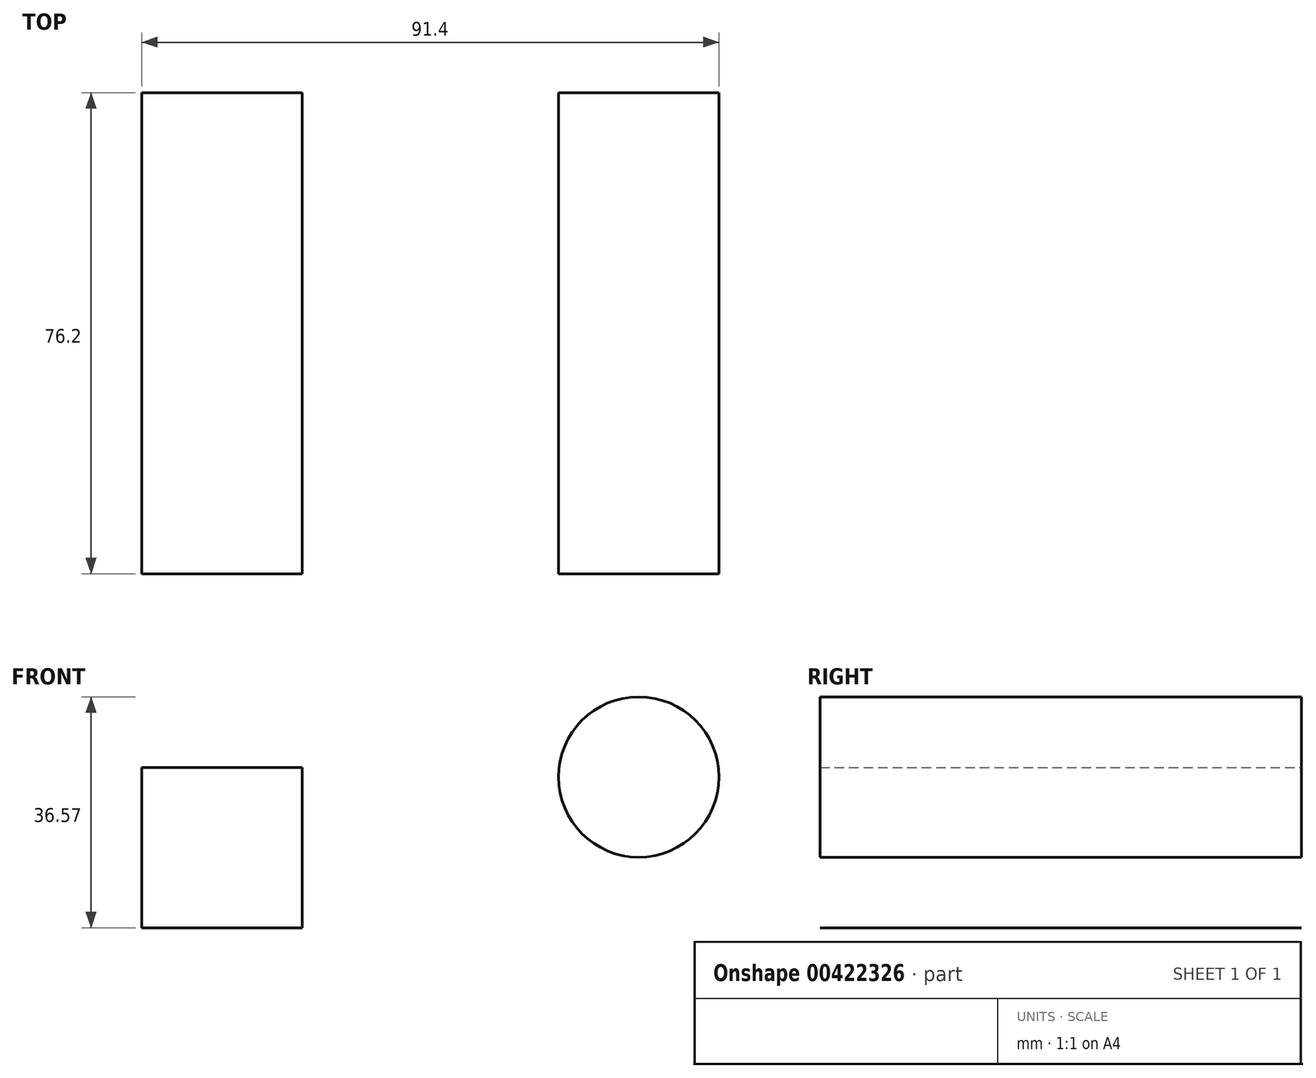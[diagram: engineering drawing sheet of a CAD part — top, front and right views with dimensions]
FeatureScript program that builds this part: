
annotation { "Feature Type Name" : "Feature", "Feature Type Description" : "" }
export const myFeature = defineFeature(function(context is Context, id is Id, definition is map)
    precondition{}
    {
        {
            var Q0;
            Q0=qCreatedBy(makeId("Front.planeOp"),FACE);
            var sketch = newSketch(context, id + "F0", { "sketchPlane" : qUnion([Q0])});
            skLineSegment(sketch, "E0", {"start": v(-54.42, 29.95) * mm, "end": v(-54.42, 4.55) * mm});
            skLineSegment(sketch, "E1", {"start": v(-54.42, 29.95) * mm, "end": v(-29.02, 29.95) * mm});
            skLineSegment(sketch, "E2", {"start": v(-29.02, 29.95) * mm, "end": v(-29.02, 4.55) * mm});
            skLineSegment(sketch, "E3", {"start": v(-54.42, 4.55) * mm, "end": v(-29.02, 4.55) * mm});
            skSolve(sketch);
        }
        {
            var Q0;
            Q0=makeQuery(id+"F0.imprint","IMPRINT",FACE,{"disambiguationData":[TD([[makeQuery(id+"F0.imprint","IMPRINT",EDGE,{"derivedFrom":sQuery(id+"F0.wireOp",EDGE,"E0")}),1.0]])]});
            extrude(context, id + "F1", {"entities" : qUnion([Q0]), "depth" : 76.2 * mm});
        }
        {
            var Q0;
            Q0=qCreatedBy(makeId("Front.planeOp"),FACE);
            var sketch = newSketch(context, id + "F2", { "sketchPlane" : qUnion([Q0])});
            skCircle(sketch, "E4", {"center": v(24.28, 28.42) * mm, "radius": 12.7 * mm});
            skSolve(sketch);
        }
        {
            var Q0;
            Q0=makeQuery(id+"F2.imprint","IMPRINT",FACE,{"disambiguationData":[TD([[makeQuery(id+"F2.imprint","IMPRINT",EDGE,{"derivedFrom":sQuery(id+"F2.wireOp",EDGE,"E4")}),1.0]])]});
            extrude(context, id + "F3", {"entities" : qUnion([Q0]), "depth" : 76.2 * mm});
        }
    });
